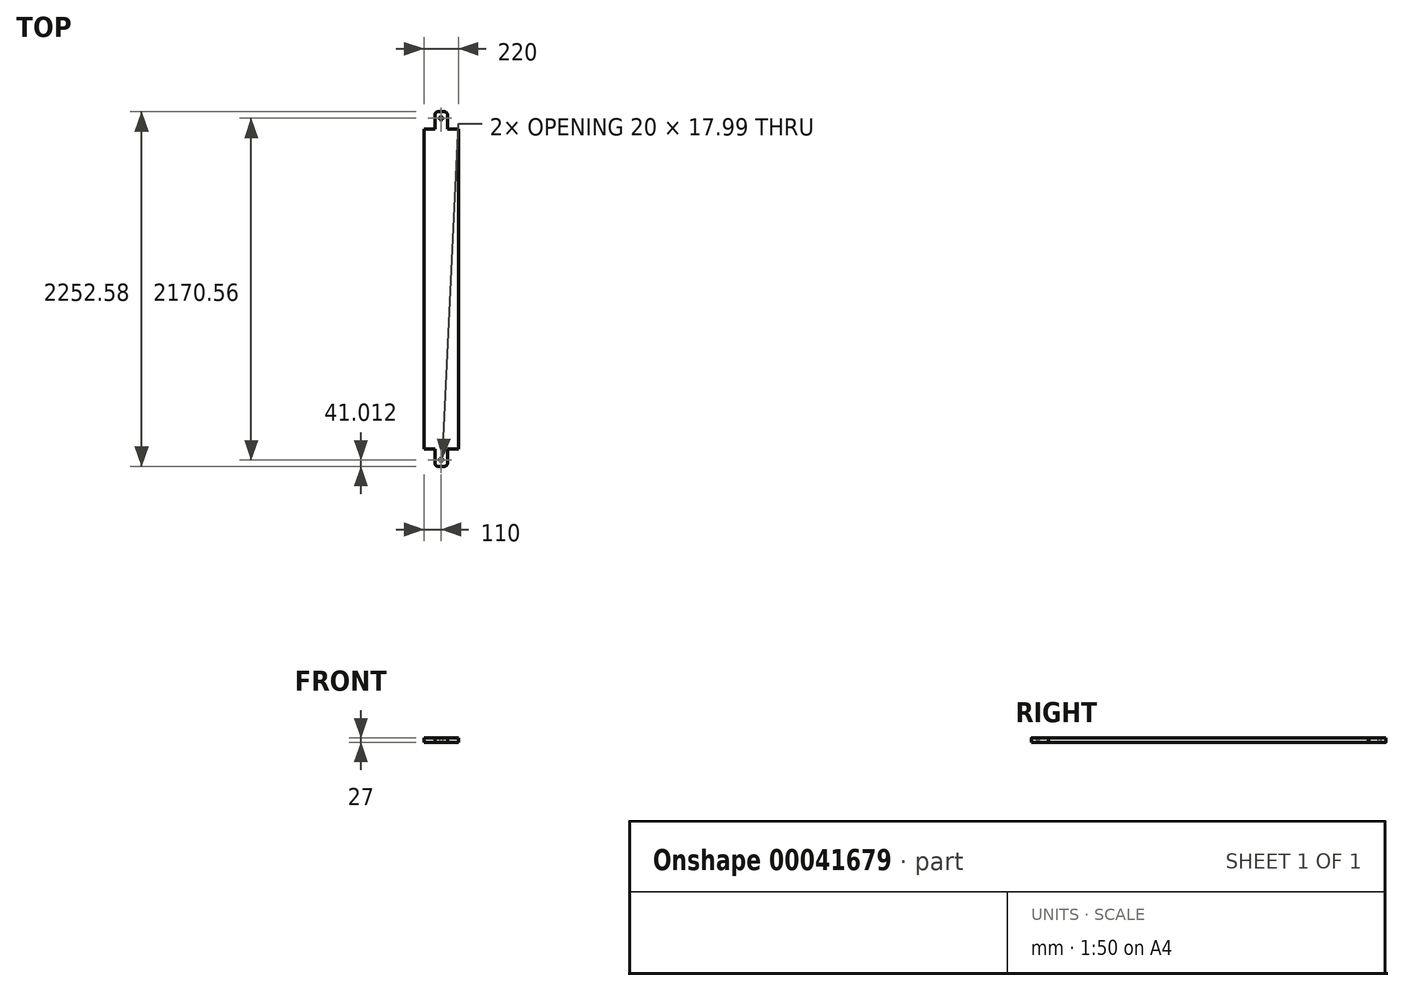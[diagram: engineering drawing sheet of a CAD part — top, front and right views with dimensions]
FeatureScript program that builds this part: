
annotation { "Feature Type Name" : "Feature", "Feature Type Description" : "" }
export const myFeature = defineFeature(function(context is Context, id is Id, definition is map)
    precondition{}
    {
        {
            var Q0;
            Q0=qCreatedBy(makeId("Top.planeOp"),FACE);
            var sketch = newSketch(context, id + "F0", { "sketchPlane" : qUnion([Q0])});
            skLineSegment(sketch, "E0", {"start": v(0, 1016) * mm, "end": v(0, 0) * mm});
            skLineSegment(sketch, "E1", {"start": v(220, 1016) * mm, "end": v(220, 0) * mm});
            skLineSegment(sketch, "E2", {"start": v(220, 0) * mm, "end": v(0, 0) * mm});
            skLineSegment(sketch, "E3", {"start": v(0, 1016) * mm, "end": v(70, 1016) * mm});
            skLineSegment(sketch, "E4", {"start": v(70, 1016) * mm, "end": v(70, 1106.29) * mm});
            skLineSegment(sketch, "E5", {"start": v(90, 1126.29) * mm, "end": v(130, 1126.29) * mm});
            skLineSegment(sketch, "E6", {"start": v(150, 1106.29) * mm, "end": v(150, 1016.29) * mm});
            skLineSegment(sketch, "E7", {"start": v(150, 1016.29) * mm, "end": v(220, 1016) * mm});
            skLineSegment(sketch, "E8", {"start": v(110, 1076.29) * mm, "end": v(100, 1076.29) * mm});
            skPoint(sketch, "E8.startSnap0", {"position": v(110, 1126.29) * mm});
            skLineSegment(sketch, "E9", {"start": v(110, 1076.29) * mm, "end": v(120, 1076.29) * mm});
            skLineSegment(sketch, "E10", {"start": v(100, 1076.29) * mm, "end": v(100, 1091.29) * mm});
            skLineSegment(sketch, "E11", {"start": v(120, 1076.29) * mm, "end": v(120, 1091.29) * mm});
            skArc(sketch, "E12", {"start": v(120, 1091.29) * mm, "mid": v(110, 1094.27) * mm, "end": v(100, 1091.29) * mm});
            skPoint(sketch, "E13.visualSharp", {"position": v(70, 1126.29) * mm});
            skArc(sketch, "E13.filletArc", {"start": v(90, 1126.29) * mm, "mid": v(75.86, 1120.43) * mm, "end": v(70, 1106.29) * mm});
            skPoint(sketch, "E14.visualSharp", {"position": v(150, 1126.29) * mm});
            skArc(sketch, "E14.filletArc", {"start": v(150, 1106.29) * mm, "mid": v(144.14, 1120.43) * mm, "end": v(130, 1126.29) * mm});
            skLineSegment(sketch, "E15.MirrorCS", {"start": v(0, -1016) * mm, "end": v(0, 0) * mm});
            skLineSegment(sketch, "E16.MirrorCS", {"start": v(0, -1016) * mm, "end": v(70, -1016) * mm});
            skLineSegment(sketch, "E17.MirrorCS", {"start": v(70, -1016) * mm, "end": v(70, -1106.29) * mm});
            skArc(sketch, "E18.MirrorCS", {"start": v(90, -1126.29) * mm, "mid": v(75.86, -1120.43) * mm, "end": v(70, -1106.29) * mm});
            skLineSegment(sketch, "E19.MirrorCS", {"start": v(90, -1126.29) * mm, "end": v(130, -1126.29) * mm});
            skArc(sketch, "E20.MirrorCS", {"start": v(150, -1106.29) * mm, "mid": v(144.14, -1120.43) * mm, "end": v(130, -1126.29) * mm});
            skLineSegment(sketch, "E21.MirrorCS", {"start": v(150, -1106.29) * mm, "end": v(150, -1016.29) * mm});
            skArc(sketch, "E22.MirrorCS", {"start": v(120, -1091.29) * mm, "mid": v(110, -1094.27) * mm, "end": v(100, -1091.29) * mm});
            skLineSegment(sketch, "E23.MirrorCS", {"start": v(100, -1076.29) * mm, "end": v(100, -1091.29) * mm});
            skLineSegment(sketch, "E24.MirrorCS", {"start": v(120, -1076.29) * mm, "end": v(120, -1091.29) * mm});
            skLineSegment(sketch, "E25.MirrorCS", {"start": v(110, -1076.29) * mm, "end": v(100, -1076.29) * mm});
            skLineSegment(sketch, "E26.MirrorCS", {"start": v(110, -1076.29) * mm, "end": v(120, -1076.29) * mm});
            skLineSegment(sketch, "E27.MirrorCS", {"start": v(150, -1016.29) * mm, "end": v(220, -1016) * mm});
            skLineSegment(sketch, "E28.MirrorCS", {"start": v(220, -1016) * mm, "end": v(220, 0) * mm});
            skSolve(sketch);
        }
        {
            var Q0;
            Q0 = qSketchRegion(id + "F0", true);
            extrude(context, id + "F1", {"entities" : qUnion([Q0]), "depth" : 27 * mm});
        }
    });
